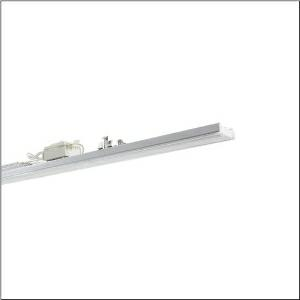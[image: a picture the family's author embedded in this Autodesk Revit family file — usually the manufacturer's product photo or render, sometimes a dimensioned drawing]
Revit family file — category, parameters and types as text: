
# Revit family: licross_r__21_recessed_ho_52te12dv4l2m3c_c3a2
name_source: partatom
category: Lighting Fixtures
units: mm (PartAtom-declared; Revit-internal decimal feet)

## family parameters
Cut with Voids When Loaded = No
Host = Face
Light Source = No
Part Type = Normal
Room Calculation Point = No
Round Connector Dimension = Use Diameter
Shared = No

## types (1)
- --- (1 x LED, 910 lm, 6.4 W, 4000K)
    Apparent Load = 6 VA
    CIE Flux Codes = 69 91 98 100 100
    Color Rendering = 80
    Color Temperature = 4000K
    Default Elevation = 1800 mm
    Description = Licross® 21 Recessed HO, luminaire insert, of sheet steel, galvanised, coil coated, white, length: 2.250mm, width: 66mm, height: 67mm, LED rated luminous flux: 22.710lm, light colour: 840, control gear: DALI 2 (for two DALI lines), with plug, 6-pole, with phase selection, for trunking rail, 14-core, mains connection: 220..240V, AC, 50/60Hz, rated input power: 129W, for trunking rail, 14-core, internal wiring halogen-free, for emergency light function, converter,control gear: single battery element, battery: LiFePO4, 9Ah, primary optical cover: cover, of PMMA, light emission: direct distribution, primary light characteristic: symmetric, protection rating (complete): IP54, insulation class (complete): insulation class I (protective earthing), certification: CE, UKCA, protection symbol: D if used in an environment with non-conductive dust loads with corresponding accessories, impact resistance: IK06, permissible ambient temperature for indoor applications: +5..+30°C, standard: EN 60598-2-22, LABS conformity tested according to VDMA 24364:2018-05, reducing of maximum allowable ambient temperature of 5°C with ceiling mounting, corresponds to IFS (International Featured Standards) requirements for safety and quality in the food industry, packaging unit: 1 piece
    Height = 58 mm
    Lamp = 1 x LED
    Lamp Light Flux = 910 lm
    Lamp Power = 6.4 W
    Lamp count = 1
    Length = 2250 mm
    Luminous efficacy = 142 lm/W
    Manufacturer = Siteco
    ModVariant = No
    Model = 52TE12DV4L2M3C
    Mounting Place = Ceiling
    Mounting Type = Pendant
    Number of Poles = 1
    OnlyDefault = Yes
    Power Factor = 1
    Product Name = Licross® 21 Recessed HO
    Product group = luminaire insert | ceiling pendant
    ProductGroupID = 902
    Protection Class = Protection class I
    Protection Degree = IP 54
    RLX_Detail_Level = 1
    RLX_Emergency_Light_Flux = 0 lm
    RLX_Emergency_Type = 0
    RLX_Emergency_Type_DB = No
    RlxData = <blob elided: 30129 chars, md5=1ca58e5a>
    Socket = socket
    Standby Power = 0 W
    System Light Flux = 910 lm
    System Power = 6 W
    Type Comments = : emergency light operation: 3 h
    Type Image = l_1296930.jpg
    URL = http://relux.com
    VarID = @adj_130763
    Voltage = 0 V
    Weight = 0.00 kg
    Width = 66 mm

## geometry (parser evidence)
native form markers: Blend x4, Sweep x9
no freeform markers — native parametric forms only
